# Revit family: Sink-Undermount-Lavatory-KOHLER-BRAZN-K-21057_1
name_source: partatom
category: Plumbing Fixtures
revit_build: Autodesk Revit 2017 (Build: 20160225_1515(x64)
units: mm (PartAtom-declared; Revit-internal decimal feet)

## family parameters
Cut with Voids When Loaded = No
Host = Face
OmniClass Number = 23.31.13.00
OmniClass Title = Sinks
Part Type = Normal
Room Calculation Point = No
Round Connector Dimension = Use Diameter
Shared = No

## types (3) — shared parameters
ADA Compliant = No
Assembly Code = D2010400
CW Connection = No
Cold Water Inlet = Cold Water Inlet
Date Modified = 12/16/2021
Default Elevation = 35"
Description = RECTANGLE UNDERCOUNTER LAVATORY
Drain Included = Yes
HW Connection = No
Height = 6 13/16"
Hot Water Inlet = Hot Water Inlet
Length = 16 3/8"
Manufacturer = KOHLER Co.
Master Format 2014 = 22 41 16
Master Format 2014 Name = Residential Lavatories and Sinks
Material = Vitreous China
Product Documentation Link = https://www.us.kohler.com
Product Name = BRAZN
Product Page URL = http://www.us.kohler.com
URL = https://www.us.kohler.com
Vent Connection = No
Waste Connection = Yes
Waste Water Outlet = Waste Water Outlet
WaterSense Certified = No
Width = 24 1/4"

## per-type parameters (varying)
| type | Finish | Model | Type |
| 0-White | Kohler-Vitreous_China-0-White | K-21057-0 | 1 |
| 58-Thunder Grey | Kohler-Vitreous_China-58-Thunder_Grey | K-21057-58 | 2 |
| HB1-Honed Black | Kohler-Vitreous_China-HB1-Honed_Black | K-21057-HB1 | 3 |

## geometry (parser evidence)
native form markers: Sweep x4
no freeform markers — native parametric forms only
